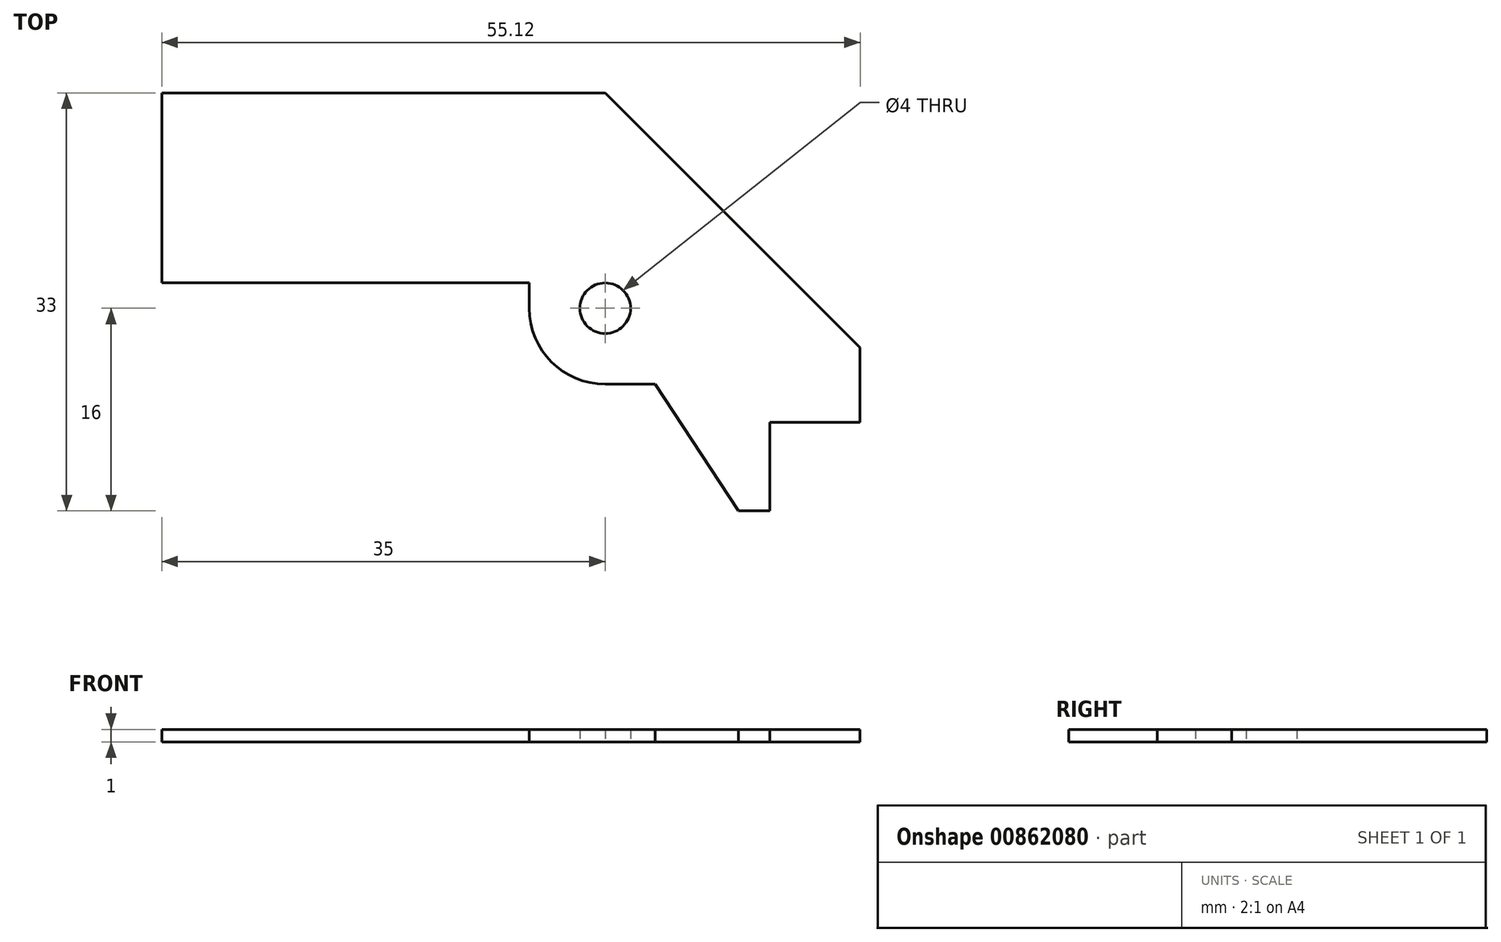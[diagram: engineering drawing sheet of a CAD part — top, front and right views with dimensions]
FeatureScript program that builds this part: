
annotation { "Feature Type Name" : "Feature", "Feature Type Description" : "" }
export const myFeature = defineFeature(function(context is Context, id is Id, definition is map)
    precondition{}
    {
        {
            var Q0;
            Q0=qCreatedBy(makeId("Top.planeOp"),FACE);
            var sketch = newSketch(context, id + "F0", { "sketchPlane" : qUnion([Q0])});
            skLineSegment(sketch, "E0", {"start": v(-35, 0) * mm, "end": v(-35, 15) * mm});
            skLineSegment(sketch, "E1", {"start": v(-35, 15) * mm, "end": v(0, 15) * mm});
            skLineSegment(sketch, "E2", {"start": v(0, 15) * mm, "end": v(20.12, -5.12) * mm});
            skLineSegment(sketch, "E3", {"start": v(10.5, 0) * mm, "end": v(10.5, -18) * mm, "construction": true});
            skLineSegment(sketch, "E4", {"start": v(10.5, -18) * mm, "end": v(3.94, -8) * mm});
            skLineSegment(sketch, "E5", {"start": v(3.94, -8) * mm, "end": v(0, -8) * mm});
            skLineSegment(sketch, "E6", {"start": v(-6, -2) * mm, "end": v(-6, 0) * mm});
            skLineSegment(sketch, "E7", {"start": v(-35, 0) * mm, "end": v(-6, 0) * mm});
            skLineSegment(sketch, "E8", {"start": v(-35, 10.7) * mm, "end": v(0, 10.7) * mm, "construction": true});
            skCircle(sketch, "E9", {"center": v(0, -2) * mm, "radius": 2 * mm});
            skLineSegment(sketch, "E10", {"start": v(0, -4) * mm, "end": v(0, -8) * mm, "construction": true});
            skLineSegment(sketch, "E11", {"start": v(0, -2) * mm, "end": v(-6, -2) * mm, "construction": true});
            skPoint(sketch, "E12.visualSharp", {"position": v(-6, -8) * mm});
            skArc(sketch, "E12.filletArc", {"start": v(-6, -2) * mm, "mid": v(-4.24, -6.24) * mm, "end": v(0, -8) * mm});
            skLineSegment(sketch, "E13", {"start": v(20.12, -5.12) * mm, "end": v(20.12, -11) * mm});
            skLineSegment(sketch, "E14", {"start": v(20.12, -11) * mm, "end": v(13, -11) * mm});
            skLineSegment(sketch, "E15", {"start": v(13, -11) * mm, "end": v(13, -18) * mm});
            skLineSegment(sketch, "E16", {"start": v(13, -18) * mm, "end": v(10.5, -18) * mm});
            skLineSegment(sketch, "E17", {"start": v(13.8, 0) * mm, "end": v(13.8, -11) * mm, "construction": true});
            skLineSegment(sketch, "E18", {"start": v(-2, -2) * mm, "end": v(-2, 8.77) * mm, "construction": true});
            skLineSegment(sketch, "E19", {"start": v(-2, 8.77) * mm, "end": v(13, 8.77) * mm, "construction": true});
            skLineSegment(sketch, "E20", {"start": v(13, 8.77) * mm, "end": v(13, -19.45) * mm, "construction": true});
            skLineSegment(sketch, "E21", {"start": v(0, -2) * mm, "end": v(10.5, -18) * mm, "construction": true});
            skSolve(sketch);
        }
        {
            var Q0;
            Q0=makeQuery(id+"F0.imprint","IMPRINT",FACE,{"disambiguationData":[TD([[makeQuery(id+"F0.imprint","IMPRINT",EDGE,{"derivedFrom":sQuery(id+"F0.wireOp",EDGE,"E0")}),-1.0]])]});
            extrude(context, id + "F1", {"entities" : qUnion([Q0]), "depth" : 1 * mm, "offsetDistance" : 25 * mm});
        }
    });
